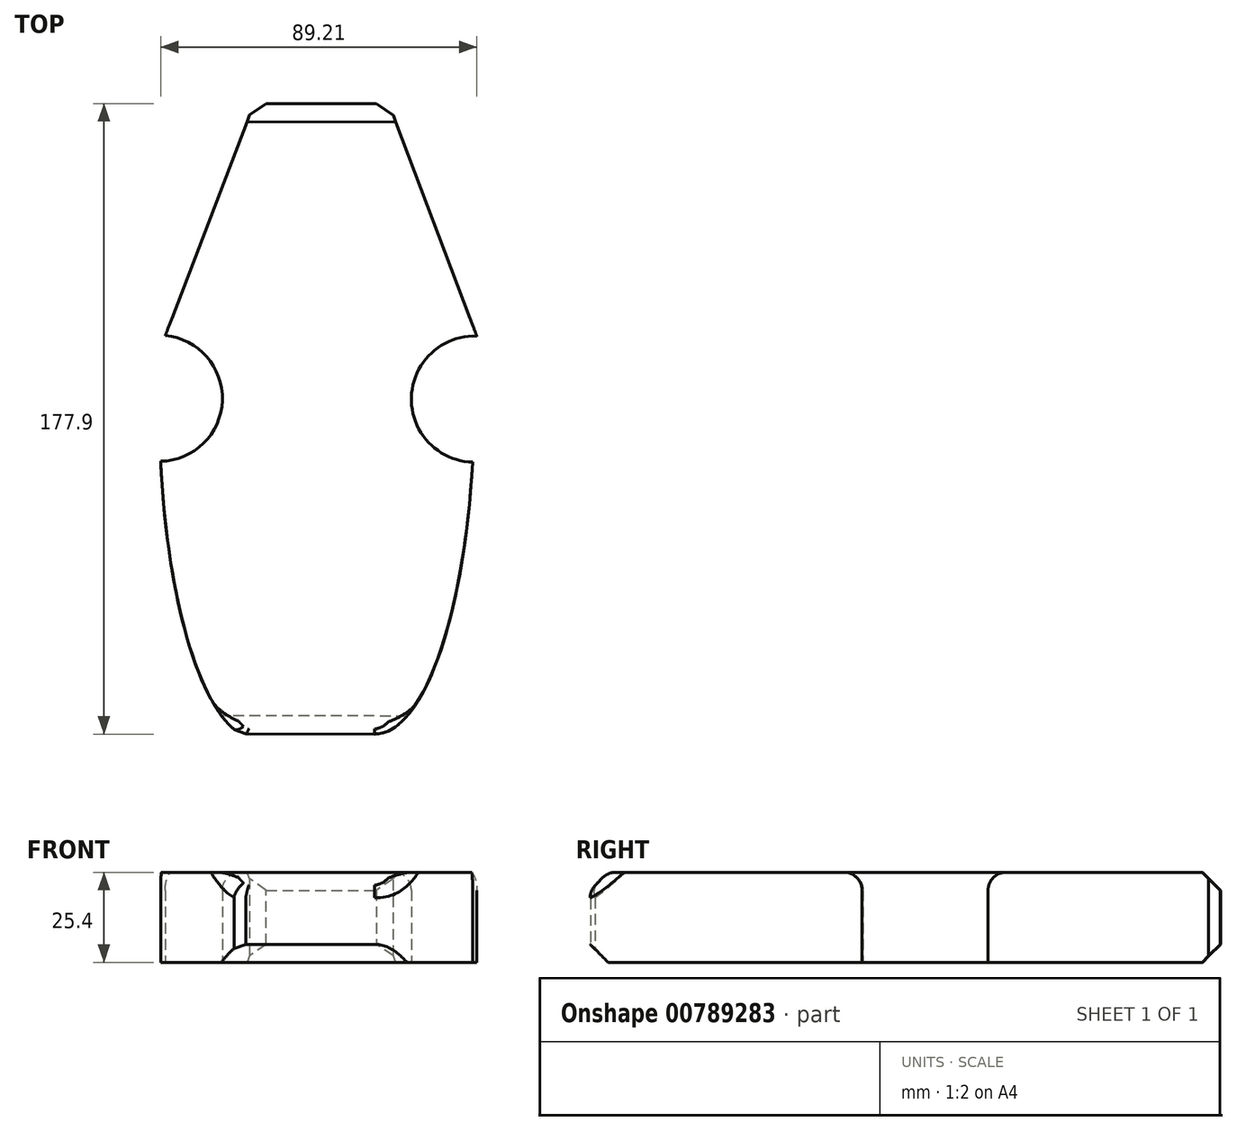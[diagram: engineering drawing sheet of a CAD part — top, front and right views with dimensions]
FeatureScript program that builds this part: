
annotation { "Feature Type Name" : "Feature", "Feature Type Description" : "" }
export const myFeature = defineFeature(function(context is Context, id is Id, definition is map)
    precondition{}
    {
        {
            var Q0;
            Q0=qCreatedBy(makeId("Top.planeOp"),FACE);
            var sketch = newSketch(context, id + "F0", { "sketchPlane" : qUnion([Q0])});
            skLineSegment(sketch, "E0.bottom", {"start": v(16.36, -94.39) * mm, "end": v(-21.74, -94.28) * mm});
            skEllipticalArc(sketch, "E1", {});
            skArc(sketch, "E2", {"start": v(-44.06, -17.42) * mm, "mid": v(-26.65, -0.3) * mm, "end": v(-42.76, 18.06) * mm});
            skEllipticalArc(sketch, "E3.trimOffspring", {});
            skArc(sketch, "E4", {"start": v(45.15, 17.88) * mm, "mid": v(26.72, 0.7) * mm, "end": v(43.99, -17.66) * mm});
            skLineSegment(sketch, "E5", {"start": v(-17.75, 83.52) * mm, "end": v(20.35, 83.41) * mm});
            skPoint(sketch, "E6.end.orphan", {"position": v(0.04, 0.23) * mm});
            skPoint(sketch, "E7.third.point.positionSnap0", {"position": v(1.3, 83.46) * mm});
            skLineSegment(sketch, "E8", {"start": v(-42.76, 18.06) * mm, "end": v(-17.75, 83.52) * mm});
            skLineSegment(sketch, "E9", {"start": v(20.35, 83.41) * mm, "end": v(45.15, 17.88) * mm});
            skPoint(sketch, "E7.center.orphan", {"position": v(1.3, 83.46) * mm});
            skLineSegment(sketch, "E10", {"start": v(-44.06, -17.42) * mm, "end": v(43.99, -17.66) * mm});
            const initialGuessF0  = {"E1": [0.01632313975052415, 0.00010082072803001351, 0.0003656917171531265, -0.9999999331347819, 0.09448893202069818, 0.028162601748285564, 0, 1.3815741946737257], "E3.trimOffspring": [-0.016319462862969595, -0.002232172170242059, -0.0005723717925814067, -0.9999998361952521, 0.09378281272756891, 0.028106833462523635, 4.875246255494602, 6.090946220222814]};
            skSetInitialGuess(sketch, initialGuessF0);
            skSolve(sketch);
        }
        {
            var Q0;
            {var subQ4=sQuery(id+"F0.wireOp",EDGE,"E0.bottom");Q0=makeQuery(id+"F0.imprint","IMPRINT",FACE,{"disambiguationData":[TD([[makeQuery(id+"F0.imprint","IMPRINT",EDGE,{"derivedFrom":subQ4}),-1.0]])]});}
            var Q1;
            {var subQ0=sQuery(id+"F0.wireOp",EDGE,"pnUStC2L-txa0-wUba-kPB3-kcAZycCMDf9Y");Q1=makeQuery(id+"F0.imprint","IMPRINT",FACE,{"disambiguationData":[TD([[makeQuery(id+"F0.imprint","IMPRINT",EDGE,{"derivedFrom":subQ0}),1.0]])]});}
            var Q2;
            {var subQ0=sQuery(id+"F0.wireOp",EDGE,"E1");Q2=makeQuery(id+"F0.imprint","IMPRINT",FACE,{"disambiguationData":[TD([[makeQuery(id+"F0.imprint","IMPRINT",EDGE,{"derivedFrom":subQ0}),1.0]])]});}
            extrude(context, id + "F1", {"entities" : qUnion([Q0, Q1, Q2]), "depth" : 25.4 * mm, "offsetDistance" : 25 * mm});
        }
        {
            var Q0;
            {var subQ0=sQuery(id+"F0.wireOp",EDGE,"E5");Q0=makeQuery(id+"F0.imprint","IMPRINT",FACE,{"disambiguationData":[TD([[makeQuery(id+"F0.imprint","IMPRINT",EDGE,{"derivedFrom":subQ0}),1.0]])]});}
            var Q1;
            {var subQ0=sQuery(id+"F0.wireOp",EDGE,"E5");Q1=makeQuery(id+"F0.imprint","IMPRINT",FACE,{"disambiguationData":[TD([[makeQuery(id+"F0.imprint","IMPRINT",EDGE,{"derivedFrom":subQ0}),-1.0]])]});}
            extrude(context, id + "F2", {"entities" : qUnion([Q0, Q1]), "operationType" : NewBodyOperationType.ADD, "depth" : 25.4 * mm, "offsetDistance" : 25.4 * mm});
        }
        {
            var Q0;
            Q0=makeQuery(id+"F2.opExtrude","CAP_EDGE",EDGE,{"disambiguationData":[OSD([sQuery(id+"F0.wireOp",EDGE,"E2")])],"isStart":false});
            var Q1;
            Q1=makeQuery(id+"F1.opExtrude","CAP_EDGE",EDGE,{"disambiguationData":[OSD([sQuery(id+"F0.wireOp",EDGE,"E2")])],"isStart":false});
            var Q2;
            Q2=makeQuery(id+"Fwnttq8RZkFdHUz_0.opExtrude","CAP_EDGE",EDGE,{"disambiguationData":[OSD([sQuery(id+"F0.wireOp",EDGE,"p7ZX8vky-u6Q4-zTXH-gQ50-eHfyUFdIPYcX")])],"isStart":false});
            var Q3;
            Q3=makeQuery(id+"F2.opExtrude","CAP_EDGE",EDGE,{"disambiguationData":[OSD([sQuery(id+"F0.wireOp",EDGE,"E4")])],"isStart":false});
            var Q4;
            Q4=makeQuery(id+"F1.opExtrude","CAP_EDGE",EDGE,{"disambiguationData":[OSD([sQuery(id+"F0.wireOp",EDGE,"E4")])],"isStart":false});
            fillet(context, id + "F3", {"entities" : qUnion([Q0, Q1, Q2, Q3, Q4]), "radius" : 5.08 * mm, "tangentPropagation" : true, "allowEdgeOverflow" : false});
        }
        {
            var Q0;
            Q0=makeQuery(id+"F2.opExtrude","SWEPT_FACE",FACE,{"disambiguationData":[OSD([sQuery(id+"F0.wireOp",EDGE,"E5")])]});
            var Q1;
            Q1=makeQuery(id+"F1.opExtrude","SWEPT_FACE",FACE,{"disambiguationData":[OSD([sQuery(id+"F0.wireOp",EDGE,"E0.bottom")])]});
            chamfer(context, id + "F4", {"entities" : qUnion([Q0, Q1]), "width" : 5.08 * mm, "tangentPropagation" : true});
        }
        {
            var Q0;
            {var subQ0=sQuery(id+"F0.wireOp",EDGE,"E0.bottom");Q0=makeQuery(id+"F4.opChamfer","BLEND_FACE",FACE,{"disambiguationData":[OSD([subQ0]),TDD([makeQuery(id+"F1.opExtrude","CAP_EDGE",EDGE,{"disambiguationData":[OSD([subQ0])],"isStart":false})])]});}
            fillet(context, id + "F5", {"entities" : qUnion([Q0]), "radius" : 5.08 * mm, "tangentPropagation" : true, "allowEdgeOverflow" : false});
        }
    });
